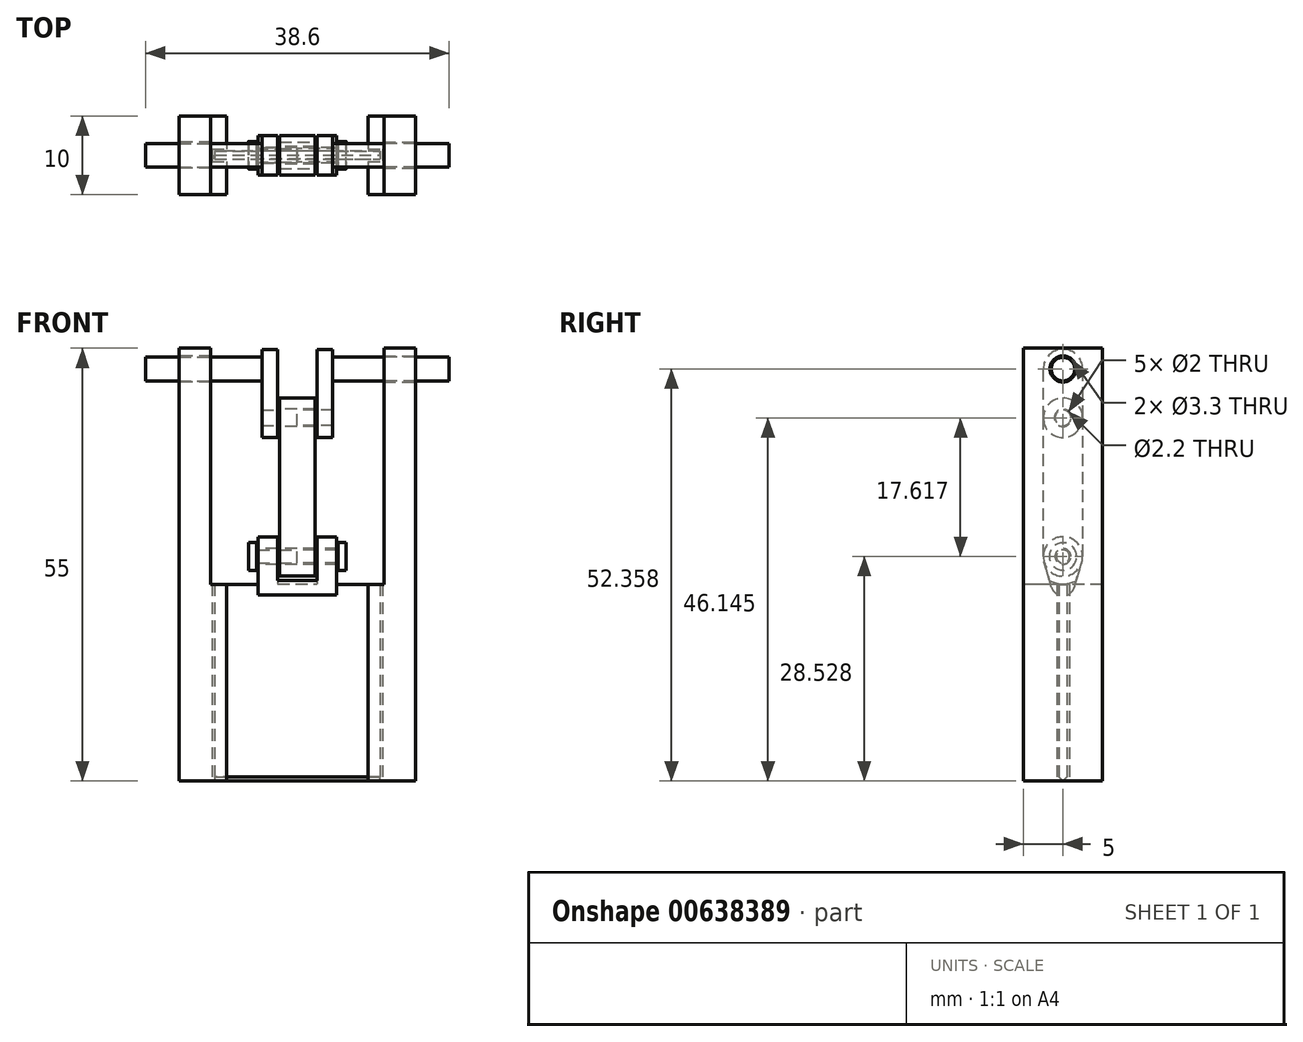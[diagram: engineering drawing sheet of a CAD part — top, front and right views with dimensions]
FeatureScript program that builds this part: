
annotation { "Feature Type Name" : "Feature", "Feature Type Description" : "" }
export const myFeature = defineFeature(function(context is Context, id is Id, definition is map)
    precondition{}
    {
        {
            var Q0;
            Q0=qCreatedBy(makeId("Top.planeOp"),FACE);
            var sketch = newSketch(context, id + "F0", { "sketchPlane" : qUnion([Q0])});
            skLineSegment(sketch, "E0.bottom", {"start": v(-15, 5) * mm, "end": v(-9, 5) * mm});
            skLineSegment(sketch, "E0.top", {"start": v(-15, -5) * mm, "end": v(-9, -5) * mm});
            skLineSegment(sketch, "E0.left", {"start": v(-15, 5) * mm, "end": v(-15, -5) * mm});
            skLineSegment(sketch, "E0.right", {"start": v(15, 5) * mm, "end": v(15, -5) * mm});
            skLineSegment(sketch, "E1.0", {"start": v(-10.5, 0.5) * mm, "end": v(10.5, 0.5) * mm});
            skLineSegment(sketch, "E1.1", {"start": v(-10.5, 0.5) * mm, "end": v(-10.5, -0.5) * mm});
            skLineSegment(sketch, "E1.2", {"start": v(-10.5, -0.5) * mm, "end": v(10.5, -0.5) * mm});
            skLineSegment(sketch, "E1.3", {"start": v(10.5, 0.5) * mm, "end": v(10.5, -0.5) * mm});
            skLineSegment(sketch, "E2.0", {"start": v(-10.8, 0.8) * mm, "end": v(-9, 0.8) * mm});
            skLineSegment(sketch, "E2.1", {"start": v(-10.8, 0.8) * mm, "end": v(-10.8, -0.8) * mm});
            skLineSegment(sketch, "E2.2", {"start": v(-10.8, -0.8) * mm, "end": v(-9, -0.8) * mm});
            skLineSegment(sketch, "E2.3", {"start": v(10.8, 0.8) * mm, "end": v(10.8, -0.8) * mm});
            skLineSegment(sketch, "E3", {"start": v(-9, 5) * mm, "end": v(-9, 0.8) * mm});
            skLineSegment(sketch, "E4", {"start": v(9, 5) * mm, "end": v(9, 0.8) * mm});
            skLineSegment(sketch, "E5.trimOffspring", {"start": v(9, 5) * mm, "end": v(15, 5) * mm});
            skLineSegment(sketch, "E6.trimOffspring", {"start": v(9, -5) * mm, "end": v(15, -5) * mm});
            skLineSegment(sketch, "E7.trimOffspring", {"start": v(-9, -0.8) * mm, "end": v(-9, -5) * mm});
            skLineSegment(sketch, "E8.trimOffspring", {"start": v(9, 0.8) * mm, "end": v(10.8, 0.8) * mm});
            skLineSegment(sketch, "E9.trimOffspring", {"start": v(9, -0.8) * mm, "end": v(10.8, -0.8) * mm});
            skLineSegment(sketch, "E10.trimOffspring", {"start": v(9, -0.8) * mm, "end": v(9, -5) * mm});
            skSolve(sketch);
        }
        {
            var Q0;
            Q0 = qSketchRegion(id + "F0", true);
            extrude(context, id + "F1", {"entities" : qUnion([Q0]), "depth" : 25 * mm, "offsetDistance" : 25 * mm});
        }
        {
            var Q0;
            Q0=makeQuery(id+"F1.opExtrude","CAP_EDGE",EDGE,{"disambiguationData":[OSD([sQuery(id+"F0.wireOp",EDGE,"E1.2")])],"isStart":true});
            var Q1;
            Q1=makeQuery(id+"F1.opExtrude","CAP_EDGE",EDGE,{"disambiguationData":[OSD([sQuery(id+"F0.wireOp",EDGE,"E1.0")])],"isStart":true});
            chamfer(context, id + "F2", {"entities" : qUnion([Q0, Q1]), "width" : .5 * mm, "tangentPropagation" : true});
        }
        {
            var Q0;
            Q0=qCreatedBy(makeId("Right.planeOp"),FACE);
            var sketch = newSketch(context, id + "F3", { "sketchPlane" : qUnion([Q0])});
            skArc(sketch, "E11", {"start": v(-1.44, 24.6) * mm, "mid": v(0, 23.53) * mm, "end": v(1.44, 24.6) * mm});
            skArc(sketch, "E12", {"start": v(2.4, 27.81) * mm, "mid": v(0, 31.03) * mm, "end": v(-2.4, 27.81) * mm});
            skCircle(sketch, "E13", {"center": v(0, 28.53) * mm, "radius": 1 * mm});
            skLineSegment(sketch, "E14", {"start": v(1.44, 24.6) * mm, "end": v(2.4, 27.81) * mm});
            skLineSegment(sketch, "E15", {"start": v(-1.44, 24.6) * mm, "end": v(-2.4, 27.81) * mm});
            skSolve(sketch);
        }
        {
            var Q0;
            Q0=makeQuery(id+"F3.imprint","IMPRINT",FACE,{"disambiguationData":[TD([[makeQuery(id+"F3.imprint","IMPRINT",EDGE,{"derivedFrom":sQuery(id+"F3.wireOp",EDGE,"E11")}),1.0]])]});
            extrude(context, id + "F4", {"entities" : qUnion([Q0]), "operationType" : NewBodyOperationType.ADD, "endBound" : BoundingType.SYMMETRIC, "depth" : 10 * mm, "offsetDistance" : 25 * mm});
        }
        {
            var Q0;
            Q0=qCreatedBy(makeId("Right.planeOp"),FACE);
            var sketch = newSketch(context, id + "F5", { "sketchPlane" : qUnion([Q0])});
            skCircle(sketch, "E16.0", {"center": v(0, 28.53) * mm, "radius": 1 * mm});
            skCircle(sketch, "E17", {"center": v(0, 28.53) * mm, "radius": 3.5 * mm});
            skSolve(sketch);
        }
        {
            var Q0;
            Q0 = qSketchRegion(id + "F5", true);
            extrude(context, id + "F6", {"entities" : qUnion([Q0]), "operationType" : NewBodyOperationType.REMOVE, "endBound" : BoundingType.SYMMETRIC, "oppositeDirection" : true, "depth" : 5 * mm, "offsetDistance" : 25 * mm});
        }
        {
            var Q0;
            Q0=qCreatedBy(makeId("Right.planeOp"),FACE);
            var sketch = newSketch(context, id + "F7", { "sketchPlane" : qUnion([Q0])});
            skCircle(sketch, "E18.0", {"center": v(0, 28.53) * mm, "radius": 0.85 * mm});
            skSolve(sketch);
        }
        {
            var Q0;
            Q0=makeQuery(id+"F7.imprint","IMPRINT",FACE,{"disambiguationData":[TD([[makeQuery(id+"F7.imprint","IMPRINT",EDGE,{"derivedFrom":sQuery(id+"F7.wireOp",EDGE,"E18.0")}),1.0]])]});
            extrude(context, id + "F8", {"entities" : qUnion([Q0]), "depth" : 5.2 * mm, "offsetDistance" : 25 * mm});
        }
        {
            var Q0;
            Q0=makeQuery(id+"F8.opExtrude","CAP_FACE",FACE,{"disambiguationData":[OSD([sQuery(id+"F7.wireOp",EDGE,"E18.0")])],"isStart":false});
            var sketch = newSketch(context, id + "F9", { "sketchPlane" : qUnion([Q0])});
            skCircle(sketch, "E19", {"center": v(0, 28.53) * mm, "radius": 1.75 * mm});
            skSolve(sketch);
        }
        {
            var Q0;
            Q0 = qSketchRegion(id + "F9", true);
            extrude(context, id + "F10", {"entities" : qUnion([Q0]), "operationType" : NewBodyOperationType.ADD, "depth" : 1 * mm, "offsetDistance" : 25 * mm});
        }
        {
            var Q0;
            Q0=makeQuery(id+"F8.opExtrude","SWEPT_BODY",BODY,{"disambiguationData":[OSD([sQuery(id+"F7.wireOp",EDGE,"E18.0")])]});
            var Q1;
            Q1=qCreatedBy(makeId("Right.planeOp"),FACE);
            mirror(context, id + "F11", {"operationType" : NewBodyOperationType.ADD, "entities" : qUnion([Q0]), "mirrorPlane" : qUnion([Q1])});
        }
        {
            var Q0;
            Q0=qCreatedBy(makeId("Right.planeOp"),FACE);
            var sketch = newSketch(context, id + "F12", { "sketchPlane" : qUnion([Q0])});
            skCircle(sketch, "E20.0", {"center": v(0, 28.53) * mm, "radius": 1 * mm});
            skArc(sketch, "E21", {"start": v(-2.5, 28.53) * mm, "mid": v(0, 26.03) * mm, "end": v(2.5, 28.53) * mm});
            skCircle(sketch, "E22", {"center": v(0, 46.14) * mm, "radius": 1.1 * mm});
            skArc(sketch, "E23", {"start": v(2.5, 46.14) * mm, "mid": v(0, 48.64) * mm, "end": v(-2.5, 46.14) * mm});
            skLineSegment(sketch, "E24", {"start": v(2.5, 46.14) * mm, "end": v(2.5, 28.53) * mm});
            skLineSegment(sketch, "E25", {"start": v(-2.5, 28.53) * mm, "end": v(-2.5, 46.14) * mm});
            skSolve(sketch);
        }
        {
            var Q0;
            Q0=makeQuery(id+"F12.imprint","IMPRINT",FACE,{"disambiguationData":[TD([[makeQuery(id+"F12.imprint","IMPRINT",EDGE,{"derivedFrom":sQuery(id+"F12.wireOp",EDGE,"E20.0")}),-1.0]])]});
            extrude(context, id + "F13", {"entities" : qUnion([Q0]), "endBound" : BoundingType.SYMMETRIC, "depth" : 4.5 * mm, "offsetDistance" : 25 * mm});
        }
        {
            var Q0;
            Q0=qCreatedBy(makeId("Right.planeOp"),FACE);
            var sketch = newSketch(context, id + "F14", { "sketchPlane" : qUnion([Q0])});
            skCircle(sketch, "E26.0", {"center": v(0, 46.14) * mm, "radius": 1 * mm});
            skSolve(sketch);
        }
        {
            var Q0;
            Q0=makeQuery(id+"F14.imprint","IMPRINT",FACE,{"disambiguationData":[TD([[makeQuery(id+"F14.imprint","IMPRINT",EDGE,{"derivedFrom":sQuery(id+"F14.wireOp",EDGE,"E26.0")}),1.0]])]});
            extrude(context, id + "F15", {"entities" : qUnion([Q0]), "depth" : 2.5 * mm, "offsetDistance" : 25 * mm});
        }
        {
            var Q0;
            Q0=makeQuery(id+"F15.opExtrude","CAP_FACE",FACE,{"disambiguationData":[OSD([sQuery(id+"F14.wireOp",EDGE,"E26.0")])],"isStart":false});
            var sketch = newSketch(context, id + "F16", { "sketchPlane" : qUnion([Q0])});
            skArc(sketch, "E27", {"start": v(-2.5, 46.14) * mm, "mid": v(0, 43.64) * mm, "end": v(2.5, 46.14) * mm});
            skArc(sketch, "E28", {"start": v(2.5, 52.34) * mm, "mid": v(0, 54.84) * mm, "end": v(-2.5, 52.34) * mm});
            skLineSegment(sketch, "E29", {"start": v(2.5, 52.34) * mm, "end": v(2.5, 46.14) * mm});
            skLineSegment(sketch, "E30", {"start": v(-2.5, 46.14) * mm, "end": v(-2.5, 52.34) * mm});
            skSolve(sketch);
        }
        {
            var Q0;
            Q0=makeQuery(id+"F16.imprint","IMPRINT",FACE,{"disambiguationData":[TD([[makeQuery(id+"F16.imprint","IMPRINT",EDGE,{"derivedFrom":sQuery(id+"F16.wireOp",EDGE,"E27")}),1.0]])]});
            extrude(context, id + "F17", {"entities" : qUnion([Q0]), "depth" : 2 * mm, "offsetDistance" : 25 * mm});
        }
        {
            var Q0;
            Q0=makeQuery(id+"F17.opExtrude","CAP_FACE",FACE,{"disambiguationData":[OSD([sQuery(id+"F14.wireOp",EDGE,"E26.0"),sQuery(id+"F16.wireOp",EDGE,"E27"),sQuery(id+"F16.wireOp",EDGE,"E28"),sQuery(id+"F16.wireOp",EDGE,"E29"),sQuery(id+"F16.wireOp",EDGE,"E30")])],"isStart":false});
            var sketch = newSketch(context, id + "F18", { "sketchPlane" : qUnion([Q0])});
            skCircle(sketch, "E31", {"center": v(0, 52.34) * mm, "radius": 1.5 * mm});
            skSolve(sketch);
        }
        {
            var Q0;
            Q0=makeQuery(id+"F18.imprint","IMPRINT",FACE,{"disambiguationData":[TD([[makeQuery(id+"F18.imprint","IMPRINT",EDGE,{"derivedFrom":sQuery(id+"F18.wireOp",EDGE,"E31")}),1.0]])]});
            extrude(context, id + "F19", {"entities" : qUnion([Q0]), "operationType" : NewBodyOperationType.ADD, "depth" : 14.8 * mm, "offsetDistance" : 25 * mm});
        }
        {
            var Q0;
            Q0=makeQuery(id+"F17.opExtrude","SWEPT_BODY",BODY,{"disambiguationData":[OSD([sQuery(id+"F14.wireOp",EDGE,"E26.0"),sQuery(id+"F16.wireOp",EDGE,"E27"),sQuery(id+"F16.wireOp",EDGE,"E28"),sQuery(id+"F16.wireOp",EDGE,"E29"),sQuery(id+"F16.wireOp",EDGE,"E30")])]});
            var Q1;
            Q1=qCreatedBy(makeId("Right.planeOp"),FACE);
            mirror(context, id + "F20", {"entities" : qUnion([Q0]), "mirrorPlane" : qUnion([Q1])});
        }
        {
            var Q0;
            Q0=makeQuery(id+"F1.opExtrude","SWEPT_FACE",FACE,{"disambiguationData":[OSD([sQuery(id+"F0.wireOp",EDGE,"E0.right")])]});
            var sketch = newSketch(context, id + "F21", { "sketchPlane" : qUnion([Q0])});
            skLineSegment(sketch, "E32.bottom", {"start": v(-5, 25) * mm, "end": v(5, 25) * mm});
            skLineSegment(sketch, "E32.top", {"start": v(-5, 55) * mm, "end": v(5, 55) * mm});
            skLineSegment(sketch, "E32.left", {"start": v(-5, 25) * mm, "end": v(-5, 55) * mm});
            skLineSegment(sketch, "E32.right", {"start": v(5, 25) * mm, "end": v(5, 55) * mm});
            skCircle(sketch, "E33", {"center": v(0, 52.36) * mm, "radius": 1.65 * mm});
            skSolve(sketch);
        }
        {
            var Q0;
            Q0 = qSketchRegion(id + "F21", true);
            extrude(context, id + "F22", {"entities" : qUnion([Q0]), "operationType" : NewBodyOperationType.ADD, "oppositeDirection" : true, "depth" : 4 * mm, "offsetDistance" : 25 * mm});
        }
        {
            var Q0;
            Q0=makeQuery(id+"F1.opExtrude","SWEPT_BODY",BODY,{"disambiguationData":[OSD([sQuery(id+"F0.wireOp",EDGE,"E0.right"),sQuery(id+"F0.wireOp",EDGE,"E2.3"),sQuery(id+"F0.wireOp",EDGE,"E4"),sQuery(id+"F0.wireOp",EDGE,"E5.trimOffspring"),sQuery(id+"F0.wireOp",EDGE,"E6.trimOffspring"),sQuery(id+"F0.wireOp",EDGE,"E8.trimOffspring"),sQuery(id+"F0.wireOp",EDGE,"E9.trimOffspring"),sQuery(id+"F0.wireOp",EDGE,"E10.trimOffspring")])]});
            var Q1;
            Q1=qCreatedBy(makeId("Right.planeOp"),FACE);
            mirror(context, id + "F23", {"operationType" : NewBodyOperationType.ADD, "entities" : qUnion([Q0]), "mirrorPlane" : qUnion([Q1])});
        }
    });
